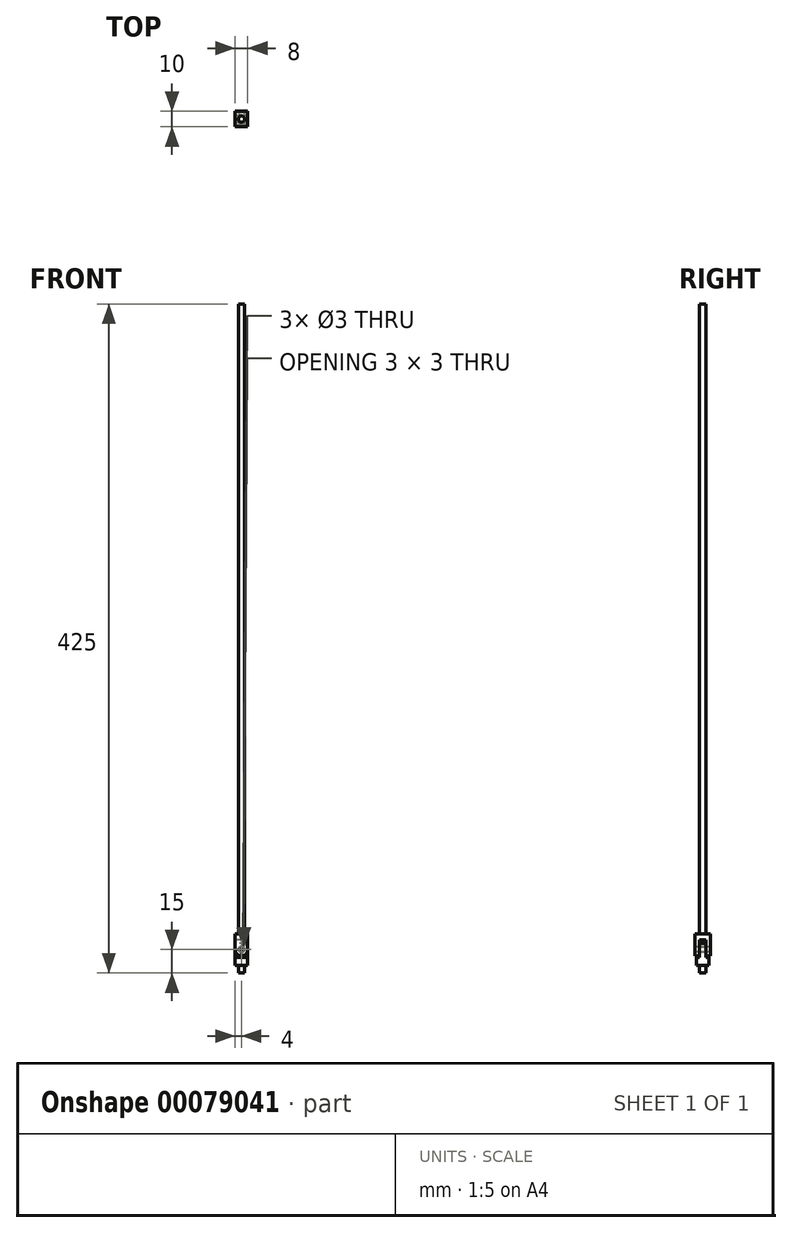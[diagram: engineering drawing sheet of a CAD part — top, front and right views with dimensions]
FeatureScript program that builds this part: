
annotation { "Feature Type Name" : "Feature", "Feature Type Description" : "" }
export const myFeature = defineFeature(function(context is Context, id is Id, definition is map)
    precondition{}
    {
        {
            var Q0;
            Q0=qCreatedBy(makeId("Front.planeOp"),FACE);
            var sketch = newSketch(context, id + "F0", { "sketchPlane" : qUnion([Q0])});
            skLineSegment(sketch, "E0.bottom", {"start": v(4, 0) * mm, "end": v(-4, 0) * mm});
            skLineSegment(sketch, "E0.top", {"start": v(4, 10) * mm, "end": v(-4, 10) * mm});
            skLineSegment(sketch, "E0.left", {"start": v(4, 0) * mm, "end": v(4, 10) * mm});
            skLineSegment(sketch, "E0.right", {"start": v(-4, 0) * mm, "end": v(-4, 10) * mm});
            skPoint(sketch, "E0.middle", {"position": v(0, 5) * mm});
            skArc(sketch, "E1", {"start": v(-4, 0) * mm, "mid": v(0, -4) * mm, "end": v(4, 0) * mm});
            skSolve(sketch);
        }
        {
            var Q0;
            Q0=makeQuery(id+"F0.imprint","IMPRINT",FACE,{"disambiguationData":[TD([[makeQuery(id+"F0.imprint","IMPRINT",EDGE,{"derivedFrom":sQuery(id+"F0.wireOp",EDGE,"E0.bottom")}),1.0]])]});
            var Q1;
            Q1=makeQuery(id+"F0.imprint","IMPRINT",FACE,{"disambiguationData":[TD([[makeQuery(id+"F0.imprint","IMPRINT",EDGE,{"derivedFrom":sQuery(id+"F0.wireOp",EDGE,"E0.bottom")}),-1.0]])]});
            extrude(context, id + "F1", {"entities" : qUnion([Q0, Q1]), "endBound" : BoundingType.SYMMETRIC, "depth" : 10 * mm});
        }
        {
            var Q0;
            Q0=makeQuery(id+"F1.opExtrude","CAP_FACE",FACE,{"disambiguationData":[OSD([sQuery(id+"F0.wireOp",EDGE,"E0.top"),sQuery(id+"F0.wireOp",EDGE,"E0.left"),sQuery(id+"F0.wireOp",EDGE,"E0.right"),sQuery(id+"F0.wireOp",EDGE,"E1")])],"isStart":false});
            var sketch = newSketch(context, id + "F2", { "sketchPlane" : qUnion([Q0])});
            skCircle(sketch, "E2", {"center": v(0, 0) * mm, "radius": 1.5 * mm});
            skSolve(sketch);
        }
        {
            var Q0;
            Q0=makeQuery(id+"F2.imprint","IMPRINT",FACE,{"disambiguationData":[TD([[makeQuery(id+"F2.imprint","IMPRINT",EDGE,{"derivedFrom":sQuery(id+"F2.wireOp",EDGE,"E2")}),1.0]])]});
            extrude(context, id + "F3", {"entities" : qUnion([Q0]), "operationType" : NewBodyOperationType.REMOVE, "endBound" : BoundingType.UP_TO_NEXT, "oppositeDirection" : true, "depth" : 25 * mm});
        }
        {
            var Q0;
            Q0=makeQuery(id+"F1.opExtrude","SWEPT_FACE",FACE,{"disambiguationData":[OSD([sQuery(id+"F0.wireOp",EDGE,"E0.right")])]});
            var sketch = newSketch(context, id + "F4", { "sketchPlane" : qUnion([Q0])});
            skLineSegment(sketch, "E3.bottom", {"start": v(2, 6) * mm, "end": v(-2, 6) * mm});
            skLineSegment(sketch, "E3.top", {"start": v(2, -4) * mm, "end": v(-2, -4) * mm});
            skLineSegment(sketch, "E3.left", {"start": v(2, 6) * mm, "end": v(2, -4) * mm});
            skLineSegment(sketch, "E3.right", {"start": v(-2, 6) * mm, "end": v(-2, -4) * mm});
            skPoint(sketch, "E3.middle", {"position": v(0, 1) * mm});
            skSolve(sketch);
        }
        {
            var Q0;
            {var subQ0=sQuery(id+"F4.wireOp",EDGE,"E3.top");Q0=makeQuery(id+"F4.imprint","IMPRINT",FACE,{"disambiguationData":[TD([[makeQuery(id+"F4.imprint","IMPRINT",EDGE,{"derivedFrom":subQ0}),-1.0]])]});}
            var Q1;
            {var subQ0=sQuery(id+"F4.wireOp",EDGE,"E3.bottom");Q1=makeQuery(id+"F4.imprint","IMPRINT",FACE,{"disambiguationData":[TD([[makeQuery(id+"F4.imprint","IMPRINT",EDGE,{"derivedFrom":subQ0}),1.0]])]});}
            extrude(context, id + "F5", {"entities" : qUnion([Q0, Q1]), "operationType" : NewBodyOperationType.REMOVE, "oppositeDirection" : true, "depth" : 25 * mm});
        }
        {
            var Q0;
            Q0=makeQuery(id+"F1.opExtrude","SWEPT_FACE",FACE,{"disambiguationData":[OSD([sQuery(id+"F0.wireOp",EDGE,"E0.top")])]});
            var sketch = newSketch(context, id + "F6", { "sketchPlane" : qUnion([Q0])});
            skCircle(sketch, "E4", {"center": v(0, 0) * mm, "radius": 2 * mm});
            skSolve(sketch);
        }
        {
            var Q0;
            Q0=makeQuery(id+"F6.imprint","IMPRINT",FACE,{"disambiguationData":[TD([[makeQuery(id+"F6.imprint","IMPRINT",EDGE,{"derivedFrom":sQuery(id+"F6.wireOp",EDGE,"E4")}),1.0]])]});
            extrude(context, id + "F7", {"entities" : qUnion([Q0]), "operationType" : NewBodyOperationType.ADD, "depth" : 400 * mm});
        }
        {
            var Q0;
            Q0=makeQuery(id+"F1.opExtrude","CAP_FACE",FACE,{"disambiguationData":[OSD([sQuery(id+"F0.wireOp",EDGE,"E0.top"),sQuery(id+"F0.wireOp",EDGE,"E0.left"),sQuery(id+"F0.wireOp",EDGE,"E0.right"),sQuery(id+"F0.wireOp",EDGE,"E1")])],"isStart":false});
            var sketch = newSketch(context, id + "F8", { "sketchPlane" : qUnion([Q0])});
            skPoint(sketch, "E5", {"position": v(-1.5, 0) * mm});
            skCircle(sketch, "E6", {"center": v(0, 0) * mm, "radius": 1.5 * mm});
            skSolve(sketch);
        }
        {
            var Q0;
            Q0=makeQuery(id+"F8.imprint","IMPRINT",FACE,{"disambiguationData":[TD([[makeQuery(id+"F8.imprint","IMPRINT",EDGE,{"derivedFrom":sQuery(id+"F8.wireOp",EDGE,"E6")}),1.0]])]});
            var Q1;
            Q1=makeQuery(id+"F1.opExtrude","CAP_FACE",FACE,{"disambiguationData":[OSD([sQuery(id+"F0.wireOp",EDGE,"E0.top"),sQuery(id+"F0.wireOp",EDGE,"E0.left"),sQuery(id+"F0.wireOp",EDGE,"E0.right"),sQuery(id+"F0.wireOp",EDGE,"E1")])],"isStart":true});
            extrude(context, id + "F9", {"entities" : qUnion([Q0]), "endBound" : BoundingType.UP_TO_SURFACE, "oppositeDirection" : true, "endBoundEntityFace" : qUnion([Q1]), "depth" : 25 * mm});
        }
        {
            var Q0;
            Q0=makeQuery(id+"F5.boolean.opBoolean","COPY",FACE,{"derivedFrom":makeQuery(id+"F5.opExtrude","SWEPT_FACE",FACE,{"disambiguationData":[OSD([sQuery(id+"F4.wireOp",EDGE,"E3.right")])]})});
            var sketch = newSketch(context, id + "F10", { "sketchPlane" : qUnion([Q0])});
            skPoint(sketch, "E7", {"position": v(-1.5, 0) * mm});
            skCircle(sketch, "E8", {"center": v(0, 0) * mm, "radius": 1.5 * mm});
            skLineSegment(sketch, "E9.bottom", {"start": v(4, 0) * mm, "end": v(-4, 0) * mm});
            skLineSegment(sketch, "E9.top", {"start": v(4, -5) * mm, "end": v(-4, -5) * mm});
            skLineSegment(sketch, "E9.left", {"start": v(4, 0) * mm, "end": v(4, -5) * mm});
            skLineSegment(sketch, "E9.right", {"start": v(-4, 0) * mm, "end": v(-4, -5) * mm});
            skPoint(sketch, "E9.middle", {"position": v(0, -2.5) * mm});
            skPoint(sketch, "E9.middle.positionSnap0", {"position": v(0, -4) * mm});
            skPoint(sketch, "E9.centerSnap0", {"position": v(0, -4) * mm});
            skArc(sketch, "E10", {"start": v(4, 0) * mm, "mid": v(0, 4) * mm, "end": v(-4, 0) * mm});
            skSolve(sketch);
        }
        {
            var Q0;
            {var subQ4=sQuery(id+"F10.wireOp",EDGE,"E10");Q0=makeQuery(id+"F10.imprint","IMPRINT",FACE,{"disambiguationData":[TD([[makeQuery(id+"F10.imprint","IMPRINT",EDGE,{"derivedFrom":subQ4}),1.0]])]});}
            var Q1;
            Q1=makeQuery(id+"F10.imprint","IMPRINT",FACE,{"disambiguationData":[TD([[makeQuery(id+"F10.imprint","IMPRINT",EDGE,{"derivedFrom":sQuery(id+"F10.wireOp",EDGE,"E9.top")}),-1.0]])]});
            var Q2;
            {var subQ5=sQuery(id+"F4.wireOp",EDGE,"E3.right");var subQ6=makeQuery(id+"F5.opExtrude","SWEPT_FACE",FACE,{"disambiguationData":[OSD([subQ5])]});var subQ7=makeQuery(id+"F5.boolean.opBoolean","INTERSECT",EDGE,{"derivedFrom":[makeQuery(id+"F1.opExtrude","SWEPT_FACE",FACE,{"disambiguationData":[OSD([sQuery(id+"F0.wireOp",EDGE,"E1")])]}),subQ6]});Q2=makeQuery(id+"F10.imprint","IMPRINT",FACE,{"disambiguationData":[TD([[makeQuery(id+"F10.imprint","IMPRINT",EDGE,{"derivedFrom":subQ7}),-1.0]])]});}
            var Q3;
            Q3=makeQuery(id+"F5.boolean.opBoolean","COPY",FACE,{"derivedFrom":makeQuery(id+"F5.opExtrude","SWEPT_FACE",FACE,{"disambiguationData":[OSD([sQuery(id+"F4.wireOp",EDGE,"E3.left")])]})});
            var Q4;
            Q4=makeQuery(id+"F1.opExtrude","SWEPT_BODY",BODY,{"disambiguationData":[OSD([sQuery(id+"F0.wireOp",EDGE,"E0.top"),sQuery(id+"F0.wireOp",EDGE,"E0.left"),sQuery(id+"F0.wireOp",EDGE,"E0.right"),sQuery(id+"F0.wireOp",EDGE,"E1")])]});
            extrude(context, id + "F11", {"entities" : qUnion([Q0, Q1, Q2]), "endBound" : BoundingType.UP_TO_SURFACE, "endBoundEntityFace" : qUnion([Q3]), "endBoundEntityBody" : qUnion([Q4]), "depth" : 25 * mm});
        }
        {
            var Q0;
            Q0=makeQuery(id+"F11.opExtrude","SWEPT_FACE",FACE,{"disambiguationData":[OSD([sQuery(id+"F10.wireOp",EDGE,"E9.top")])]});
            var sketch = newSketch(context, id + "F12", { "sketchPlane" : qUnion([Q0])});
            skLineSegment(sketch, "E11.bottom", {"start": v(4, -4) * mm, "end": v(-4, -4) * mm});
            skLineSegment(sketch, "E11.top", {"start": v(4, 4) * mm, "end": v(-4, 4) * mm});
            skLineSegment(sketch, "E11.left", {"start": v(4, -4) * mm, "end": v(4, 4) * mm});
            skLineSegment(sketch, "E11.right", {"start": v(-4, -4) * mm, "end": v(-4, 4) * mm});
            skPoint(sketch, "E11.middle", {"position": v(0, 0) * mm});
            skCircle(sketch, "E12", {"center": v(0, 0) * mm, "radius": 2 * mm});
            skSolve(sketch);
        }
        {
            var Q0;
            {var subQ0=sQuery(id+"F12.wireOp",EDGE,"E12");var subQ1=sQuery(id+"F10.wireOp",EDGE,"E9.top");var subQ2=makeQuery(id+"F12.imprint","INTERSECT",VERTEX,{"derivedFrom":[makeQuery(id+"F11.opExtrude","CAP_EDGE",EDGE,{"disambiguationData":[OSD([subQ1])],"isStart":true}),subQ0]});Q0=makeQuery(id+"F12.imprint","IMPRINT",FACE,{"disambiguationData":[TD([[makeQuery(id+"F12.imprint","IMPRINT",EDGE,{"disambiguationData":[TD([[subQ2,1.0]])],"derivedFrom":subQ0}),1.0]])]});}
            var Q1;
            Q1=sQuery(id+"F12.wireOp",EDGE,"E11.bottom");
            var Q2;
            Q2=sQuery(id+"F12.wireOp",EDGE,"E11.left");
            var Q3;
            Q3=sQuery(id+"F12.wireOp",EDGE,"E11.right");
            var Q4;
            Q4=sQuery(id+"F12.wireOp",EDGE,"E11.top");
            extrude(context, id + "F13", {"entities" : qUnion([Q0]), "operationType" : NewBodyOperationType.ADD, "surfaceEntities" : qUnion([Q1, Q2, Q3, Q4]), "depth" : 10 * mm});
        }
        {
            var Q0;
            {var subQ6=sQuery(id+"F12.wireOp",EDGE,"E11.bottom");Q0=makeQuery(id+"F12.imprint","IMPRINT",FACE,{"disambiguationData":[TD([[makeQuery(id+"F12.imprint","IMPRINT",EDGE,{"derivedFrom":subQ6}),-1.0]])]});}
            var Q1;
            {var subQ6=sQuery(id+"F12.wireOp",EDGE,"E11.top");Q1=makeQuery(id+"F12.imprint","IMPRINT",FACE,{"disambiguationData":[TD([[makeQuery(id+"F12.imprint","IMPRINT",EDGE,{"derivedFrom":subQ6}),1.0]])]});}
            var Q2;
            {var subQ0=sQuery(id+"F12.wireOp",EDGE,"E11.left");var subQ1=sQuery(id+"F10.wireOp",EDGE,"E9.top");var subQ2=makeQuery(id+"F11.opExtrude","CAP_EDGE",EDGE,{"disambiguationData":[OSD([subQ1])],"isStart":true});var subQ3=makeQuery(id+"F12.imprint","INTERSECT",VERTEX,{"derivedFrom":[subQ2,subQ0]});var subQ4=makeQuery(id+"F11.opExtrude","CAP_EDGE",EDGE,{"disambiguationData":[OSD([subQ1])],"isStart":false});var subQ5=makeQuery(id+"F12.imprint","INTERSECT",VERTEX,{"derivedFrom":[subQ4,subQ0]});Q2=makeQuery(id+"F12.imprint","IMPRINT",FACE,{"disambiguationData":[TD([[makeQuery(id+"F12.imprint","IMPRINT",EDGE,{"disambiguationData":[TD([[subQ3,1.0],[subQ5,-1.0]])],"derivedFrom":subQ0}),-1.0]])]});}
            var Q3;
            {var subQ0=sQuery(id+"F12.wireOp",EDGE,"E11.right");var subQ1=sQuery(id+"F10.wireOp",EDGE,"E9.top");var subQ2=makeQuery(id+"F11.opExtrude","CAP_EDGE",EDGE,{"disambiguationData":[OSD([subQ1])],"isStart":true});var subQ3=makeQuery(id+"F12.imprint","INTERSECT",VERTEX,{"derivedFrom":[subQ2,subQ0]});var subQ4=makeQuery(id+"F11.opExtrude","CAP_EDGE",EDGE,{"disambiguationData":[OSD([subQ1])],"isStart":false});var subQ5=makeQuery(id+"F12.imprint","INTERSECT",VERTEX,{"derivedFrom":[subQ4,subQ0]});Q3=makeQuery(id+"F12.imprint","IMPRINT",FACE,{"disambiguationData":[TD([[makeQuery(id+"F12.imprint","IMPRINT",EDGE,{"disambiguationData":[TD([[subQ3,1.0],[subQ5,-1.0]])],"derivedFrom":subQ0}),1.0]])]});}
            extrude(context, id + "F14", {"entities" : qUnion([Q0, Q1, Q2, Q3]), "operationType" : NewBodyOperationType.ADD, "depth" : 5 * mm});
        }
    });
